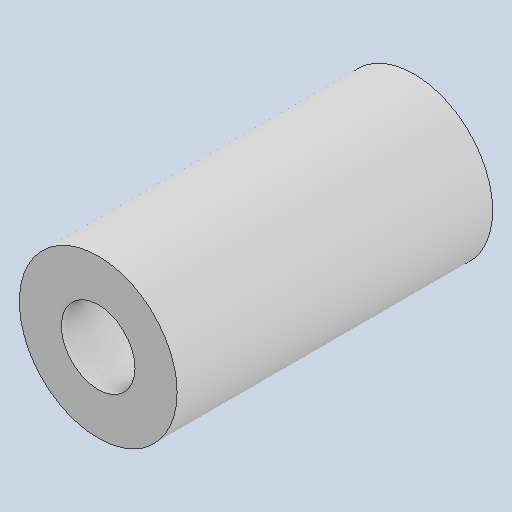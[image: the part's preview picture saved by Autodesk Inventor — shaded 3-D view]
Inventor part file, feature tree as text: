
AUTODESK INVENTOR PART (.ipt)
format: ipt  version: 2024 (Build 280153000, 153)  size: 100,352 bytes
history: native  units: in
note: dims shown in document units (in); Inventor stores cm internally (conversion verified against a paired STEP export)
features: extrude x1, sketch x1
ambient origin geometry x8: Origin, YZ Plane, XZ Plane, XY Plane, X Axis, Y Axis, Z Axis, Center Point
bodies: Solid1 (feature_tree)
feature tree (2):
  extrude  "Extrusion1"  Depth=0.75in
  sketch  "Sketch1"  dims[d0=0.175in d1=0.1in d2=0.75in d3=0.0in]
